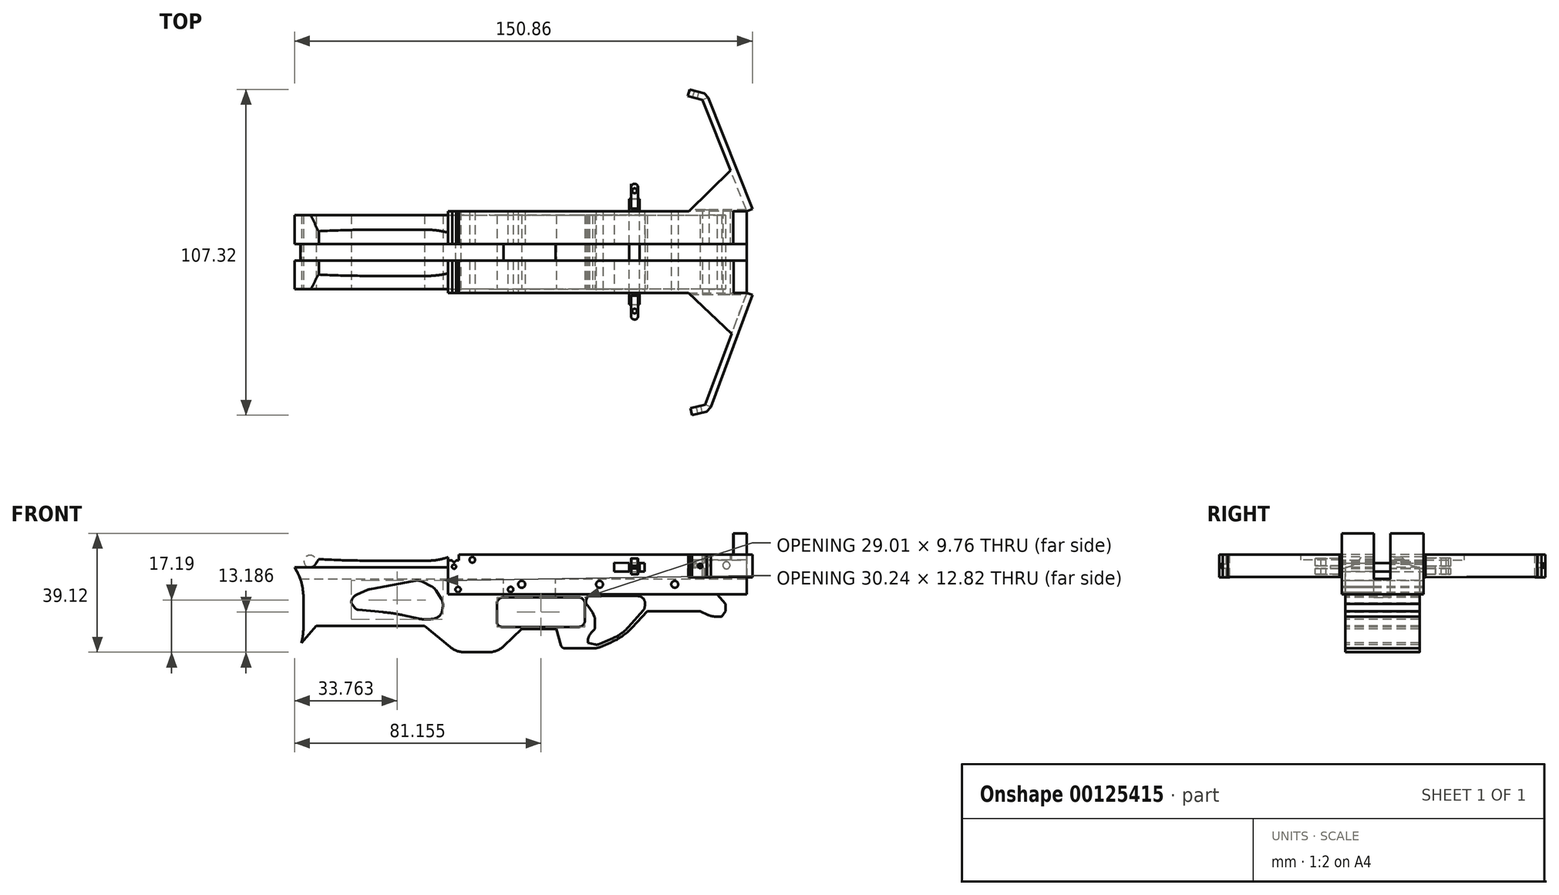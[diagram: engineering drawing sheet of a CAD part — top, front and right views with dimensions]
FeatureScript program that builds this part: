
annotation { "Feature Type Name" : "Feature", "Feature Type Description" : "" }
export const myFeature = defineFeature(function(context is Context, id is Id, definition is map)
    precondition{}
    {
        {
            var Q0;
            Q0=qCreatedBy(makeId("Top.planeOp"),FACE);
            var sketch = newSketch(context, id + "F0", { "sketchPlane" : qUnion([Q0])});
            skLineSegment(sketch, "E0", {"start": v(-24.32, 26.9) * mm, "end": v(-24.32, 0) * mm});
            skLineSegment(sketch, "E1", {"start": v(-24.32, 0) * mm, "end": v(74.17, 0) * mm});
            skLineSegment(sketch, "E2", {"start": v(74.17, 0) * mm, "end": v(74.17, 26.9) * mm});
            skLineSegment(sketch, "E3", {"start": v(74.17, 26.9) * mm, "end": v(-24.32, 26.9) * mm});
            skSolve(sketch);
        }
        {
            var Q0;
            Q0 = qSketchRegion(id + "F0", true);
            extrude(context, id + "F1", {"entities" : qUnion([Q0]), "depth" : 13 * mm});
        }
        {
            var Q0;
            Q0=makeQuery(id+"F1.opExtrude","CAP_FACE",FACE,{"disambiguationData":[OSD([sQuery(id+"F0.wireOp",EDGE,"E0"),sQuery(id+"F0.wireOp",EDGE,"E1"),sQuery(id+"F0.wireOp",EDGE,"E2"),sQuery(id+"F0.wireOp",EDGE,"E3")])],"isStart":false});
            var sketch = newSketch(context, id + "F2", { "sketchPlane" : qUnion([Q0])});
            skLineSegment(sketch, "E4.bottom", {"start": v(-24.32, 16.02) * mm, "end": v(74.17, 16.02) * mm});
            skLineSegment(sketch, "E4.top", {"start": v(-24.32, 10.62) * mm, "end": v(74.17, 10.62) * mm});
            skLineSegment(sketch, "E4.left", {"start": v(-24.32, 16.02) * mm, "end": v(-24.32, 10.62) * mm});
            skLineSegment(sketch, "E4.right", {"start": v(74.17, 16.02) * mm, "end": v(74.17, 10.62) * mm});
            skSolve(sketch);
        }
        {
            var Q0;
            Q0 = qSketchRegion(id + "F2", true);
            extrude(context, id + "F3", {"entities" : qUnion([Q0]), "operationType" : NewBodyOperationType.REMOVE, "oppositeDirection" : true, "depth" : 8 * mm});
        }
        {
            var Q0;
            Q0=makeQuery(id+"F1.opExtrude","SWEPT_FACE",FACE,{"disambiguationData":[OSD([sQuery(id+"F0.wireOp",EDGE,"E1")])]});
            var sketch = newSketch(context, id + "F4", { "sketchPlane" : qUnion([Q0])});
            skLineSegment(sketch, "E5", {"start": v(30.43, 10.33) * mm, "end": v(30.43, 7.4) * mm});
            skLineSegment(sketch, "E6", {"start": v(30.43, 7.4) * mm, "end": v(40.53, 7.4) * mm});
            skLineSegment(sketch, "E7", {"start": v(40.53, 7.4) * mm, "end": v(40.53, 10.23) * mm});
            skLineSegment(sketch, "E8", {"start": v(40.53, 10.23) * mm, "end": v(30.43, 10.33) * mm});
            skSolve(sketch);
        }
        {
            var Q0;
            Q0 = qSketchRegion(id + "F4", true);
            extrude(context, id + "F5", {"entities" : qUnion([Q0]), "operationType" : NewBodyOperationType.REMOVE, "oppositeDirection" : true, "depth" : 30 * mm});
        }
        {
            var Q0;
            Q0=makeQuery(id+"F1.opExtrude","SWEPT_FACE",FACE,{"disambiguationData":[OSD([sQuery(id+"F0.wireOp",EDGE,"E1")])]});
            var sketch = newSketch(context, id + "F6", { "sketchPlane" : qUnion([Q0])});
            skLineSegment(sketch, "E9", {"start": v(57.11, 13) * mm, "end": v(57.11, 5.6) * mm});
            skLineSegment(sketch, "E10", {"start": v(57.11, 5.6) * mm, "end": v(74.17, 5.6) * mm});
            skLineSegment(sketch, "E11", {"start": v(74.17, 5.6) * mm, "end": v(74.17, 13) * mm});
            skLineSegment(sketch, "E12", {"start": v(74.17, 13) * mm, "end": v(57.11, 13) * mm});
            skSolve(sketch);
        }
        {
            var Q0;
            Q0 = qSketchRegion(id + "F6", true);
            extrude(context, id + "F7", {"entities" : qUnion([Q0]), "operationType" : NewBodyOperationType.ADD, "depth" : 0.5 * mm});
        }
        {
            var Q0;
            Q0=makeQuery(id+"F1.opExtrude","SWEPT_FACE",FACE,{"disambiguationData":[OSD([sQuery(id+"F0.wireOp",EDGE,"E3")])]});
            var sketch = newSketch(context, id + "F8", { "sketchPlane" : qUnion([Q0])});
            skLineSegment(sketch, "E13", {"start": v(-74.17, 13) * mm, "end": v(-74.17, 5.6) * mm});
            skLineSegment(sketch, "E14", {"start": v(-74.17, 5.6) * mm, "end": v(-55.11, 5.6) * mm});
            skLineSegment(sketch, "E15", {"start": v(-55.11, 5.6) * mm, "end": v(-55.11, 13) * mm});
            skLineSegment(sketch, "E16", {"start": v(-55.11, 13) * mm, "end": v(-74.17, 13) * mm});
            skSolve(sketch);
        }
        {
            var Q0;
            Q0 = qSketchRegion(id + "F8", true);
            extrude(context, id + "F9", {"entities" : qUnion([Q0]), "operationType" : NewBodyOperationType.ADD, "depth" : 0.5 * mm});
        }
        {
            var Q0;
            Q0=makeQuery(id+"F7.opExtrude","CAP_FACE",FACE,{"disambiguationData":[OSD([sQuery(id+"F6.wireOp",EDGE,"E9"),sQuery(id+"F6.wireOp",EDGE,"E10"),sQuery(id+"F6.wireOp",EDGE,"E11"),sQuery(id+"F6.wireOp",EDGE,"E12")])],"isStart":false});
            var sketch = newSketch(context, id + "F10", { "sketchPlane" : qUnion([Q0])});
            skCircle(sketch, "E17", {"center": v(60.6, 9.48) * mm, "radius": 1.05 * mm});
            skCircle(sketch, "E18", {"center": v(67.47, 9.48) * mm, "radius": 1.18 * mm});
            skSolve(sketch);
        }
        {
            var Q0;
            Q0 = qSketchRegion(id + "F10", true);
            extrude(context, id + "F11", {"entities" : qUnion([Q0]), "operationType" : NewBodyOperationType.REMOVE, "oppositeDirection" : true, "depth" : 28.5 * mm});
        }
        {
            var Q0;
            Q0=makeQuery(id+"F1.opExtrude","SWEPT_FACE",FACE,{"disambiguationData":[OSD([sQuery(id+"F0.wireOp",EDGE,"E1")])]});
            var sketch = newSketch(context, id + "F12", { "sketchPlane" : qUnion([Q0])});
            skCircle(sketch, "E19", {"center": v(-20.96, 1.54) * mm, "radius": 0.9 * mm});
            skCircle(sketch, "E20", {"center": v(-3.64, 1.54) * mm, "radius": 0.9 * mm});
            skCircle(sketch, "E21", {"center": v(0, 3.23) * mm, "radius": 1.15 * mm});
            skCircle(sketch, "E22", {"center": v(25.65, 3.23) * mm, "radius": 1.14 * mm});
            skCircle(sketch, "E23", {"center": v(50.44, 3.23) * mm, "radius": 1.14 * mm});
            skSolve(sketch);
        }
        {
            var Q0;
            Q0 = qSketchRegion(id + "F12", true);
            extrude(context, id + "F13", {"entities" : qUnion([Q0]), "operationType" : NewBodyOperationType.REMOVE, "oppositeDirection" : true, "depth" : 28.5 * mm});
        }
        {
            var Q0;
            Q0=makeQuery(id+"F1.opExtrude","SWEPT_FACE",FACE,{"disambiguationData":[OSD([sQuery(id+"F0.wireOp",EDGE,"E3")])]});
            var sketch = newSketch(context, id + "F14", { "sketchPlane" : qUnion([Q0])});
            skLineSegment(sketch, "E24", {"start": v(-38.9, 10.24) * mm, "end": v(-38.87, 7.4) * mm});
            skPoint(sketch, "E24.endSnap0", {"position": v(-35.48, 7.4) * mm});
            skLineSegment(sketch, "E25", {"start": v(-38.87, 7.4) * mm, "end": v(-35.48, 7.4) * mm});
            skLineSegment(sketch, "E26", {"start": v(-35.48, 7.4) * mm, "end": v(-35.48, 10.28) * mm});
            skLineSegment(sketch, "E27", {"start": v(-35.48, 10.28) * mm, "end": v(-38.9, 10.24) * mm});
            skSolve(sketch);
        }
        {
            var Q0;
            Q0 = qSketchRegion(id + "F14", true);
            extrude(context, id + "F15", {"entities" : qUnion([Q0]), "operationType" : NewBodyOperationType.ADD, "oppositeDirection" : true, "depth" : 26.9 * mm});
        }
        {
            var Q0;
            Q0=makeQuery(id+"F15.boolean.opBoolean","MERGE",FACE,{"derivedFrom":[makeQuery(id+"F1.opExtrude","SWEPT_FACE",FACE,{"disambiguationData":[OSD([sQuery(id+"F0.wireOp",EDGE,"E3")])]}),makeQuery(id+"F15.opExtrude","CAP_FACE",FACE,{"disambiguationData":[OSD([sQuery(id+"F14.wireOp",EDGE,"E24"),sQuery(id+"F14.wireOp",EDGE,"E25"),sQuery(id+"F14.wireOp",EDGE,"E26"),sQuery(id+"F14.wireOp",EDGE,"E27")])],"isStart":true})]});
            var sketch = newSketch(context, id + "F16", { "sketchPlane" : qUnion([Q0])});
            skLineSegment(sketch, "E28.bottom", {"start": v(-38.9, 9.28) * mm, "end": v(-35.48, 9.28) * mm});
            skLineSegment(sketch, "E28.top", {"start": v(-38.9, 8.44) * mm, "end": v(-35.48, 8.44) * mm});
            skLineSegment(sketch, "E28.left", {"start": v(-38.9, 9.28) * mm, "end": v(-38.9, 8.44) * mm});
            skLineSegment(sketch, "E28.right", {"start": v(-35.48, 9.28) * mm, "end": v(-35.48, 8.44) * mm});
            skSolve(sketch);
        }
        {
            var Q0;
            Q0 = qSketchRegion(id + "F16", true);
            extrude(context, id + "F17", {"entities" : qUnion([Q0]), "operationType" : NewBodyOperationType.ADD, "depth" : 4 * mm});
        }
        {
            var Q0;
            Q0=makeQuery(id+"F17.opExtrude","SWEPT_FACE",FACE,{"disambiguationData":[OSD([sQuery(id+"F16.wireOp",EDGE,"E28.bottom")])]});
            var sketch = newSketch(context, id + "F18", { "sketchPlane" : qUnion([Q0])});
            skSolve(sketch);
        }
        {
            var Q0;
            {var subQ0=sQuery(id+"F16.wireOp",EDGE,"E28.bottom");Q0=makeQuery(id+"F18.imprint","IMPRINT",FACE,{"disambiguationData":[TD([[makeQuery(id+"F18.imprint","IMPRINT",EDGE,{"derivedFrom":makeQuery(id+"F17.opExtrude","CAP_EDGE",EDGE,{"disambiguationData":[OSD([subQ0])],"isStart":false})}),1.0]])]});}
            var sketch = newSketch(context, id + "F19", { "sketchPlane" : qUnion([Q0])});
            skLineSegment(sketch, "E29", {"start": v(38.29, 30.89) * mm, "end": v(38.29, 27.83) * mm});
            skLineSegment(sketch, "E30", {"start": v(38.16, 27.7) * mm, "end": v(36.22, 27.7) * mm});
            skLineSegment(sketch, "E31", {"start": v(36.1, 27.83) * mm, "end": v(36.1, 30.88) * mm});
            skLineSegment(sketch, "E32", {"start": v(36.1, 30.88) * mm, "end": v(38.29, 30.89) * mm});
            skPoint(sketch, "E33.visualSharp", {"position": v(38.29, 27.7) * mm});
            skArc(sketch, "E33.filletArc", {"start": v(38.16, 27.7) * mm, "mid": v(38.25, 27.74) * mm, "end": v(38.29, 27.83) * mm});
            skPoint(sketch, "E34.visualSharp", {"position": v(36.1, 27.7) * mm});
            skArc(sketch, "E34.filletArc", {"start": v(36.1, 27.83) * mm, "mid": v(36.13, 27.74) * mm, "end": v(36.22, 27.7) * mm});
            skSolve(sketch);
        }
        {
            var Q0;
            Q0=makeQuery(id+"F15.opExtrude","CAP_FACE",FACE,{"disambiguationData":[OSD([sQuery(id+"F14.wireOp",EDGE,"E24"),sQuery(id+"F14.wireOp",EDGE,"E25"),sQuery(id+"F14.wireOp",EDGE,"E26"),sQuery(id+"F14.wireOp",EDGE,"E27")])],"isStart":false});
            var sketch = newSketch(context, id + "F20", { "sketchPlane" : qUnion([Q0])});
            skLineSegment(sketch, "E35.bottom", {"start": v(35.48, 9.32) * mm, "end": v(38.88, 9.32) * mm});
            skLineSegment(sketch, "E35.top", {"start": v(35.48, 8.45) * mm, "end": v(38.88, 8.45) * mm});
            skLineSegment(sketch, "E35.left", {"start": v(35.48, 9.32) * mm, "end": v(35.48, 8.45) * mm});
            skLineSegment(sketch, "E35.right", {"start": v(38.88, 9.32) * mm, "end": v(38.88, 8.45) * mm});
            skSolve(sketch);
        }
        {
            var Q0;
            Q0 = qSketchRegion(id + "F20", true);
            extrude(context, id + "F21", {"entities" : qUnion([Q0]), "operationType" : NewBodyOperationType.ADD, "depth" : 3.8 * mm});
        }
        {
            var Q0;
            Q0=makeQuery(id+"F21.opExtrude","SWEPT_FACE",FACE,{"disambiguationData":[OSD([sQuery(id+"F20.wireOp",EDGE,"E35.bottom")])]});
            var sketch = newSketch(context, id + "F22", { "sketchPlane" : qUnion([Q0])});
            skLineSegment(sketch, "E36", {"start": v(36.04, -3.8) * mm, "end": v(36.04, -1.03) * mm});
            skLineSegment(sketch, "E37", {"start": v(36.17, -0.9) * mm, "end": v(38.18, -0.9) * mm});
            skLineSegment(sketch, "E38", {"start": v(38.3, -1.03) * mm, "end": v(38.3, -3.8) * mm});
            skLineSegment(sketch, "E39", {"start": v(38.3, -3.8) * mm, "end": v(36.04, -3.8) * mm});
            skPoint(sketch, "E40.visualSharp", {"position": v(36.04, -0.9) * mm});
            skArc(sketch, "E40.filletArc", {"start": v(36.17, -0.9) * mm, "mid": v(36.08, -0.94) * mm, "end": v(36.04, -1.03) * mm});
            skPoint(sketch, "E41.visualSharp", {"position": v(38.3, -0.9) * mm});
            skArc(sketch, "E41.filletArc", {"start": v(38.3, -1.03) * mm, "mid": v(38.27, -0.94) * mm, "end": v(38.18, -0.9) * mm});
            skSolve(sketch);
        }
        {
            var Q0;
            Q0 = qSketchRegion(id + "F22", true);
            extrude(context, id + "F23", {"entities" : qUnion([Q0]), "operationType" : NewBodyOperationType.ADD, "depth" : 2.4 * mm, "hasSecondDirection" : true, "secondDirectionOppositeDirection" : true, "secondDirectionDepth" : 2.8 * mm});
        }
        {
            var Q0;
            Q0 = qSketchRegion(id + "F19", true);
            extrude(context, id + "F24", {"entities" : qUnion([Q0]), "operationType" : NewBodyOperationType.ADD, "depth" : 2.6 * mm, "hasSecondDirection" : true, "secondDirectionOppositeDirection" : true, "secondDirectionDepth" : 2.75 * mm});
        }
        {
            var Q0;
            Q0=makeQuery(id+"F23.boolean.opBoolean","MERGE",FACE,{"derivedFrom":[makeQuery(id+"F21.opExtrude","CAP_FACE",FACE,{"disambiguationData":[OSD([sQuery(id+"F20.wireOp",EDGE,"E35.bottom"),sQuery(id+"F20.wireOp",EDGE,"E35.top"),sQuery(id+"F20.wireOp",EDGE,"E35.left"),sQuery(id+"F20.wireOp",EDGE,"E35.right")])],"isStart":false}),makeQuery(id+"F23.opExtrude","SWEPT_FACE",FACE,{"disambiguationData":[OSD([sQuery(id+"F22.wireOp",EDGE,"E39")])]})]});
            var sketch = newSketch(context, id + "F25", { "sketchPlane" : qUnion([Q0])});
            skLineSegment(sketch, "E42", {"start": v(36.04, 9.32) * mm, "end": v(38.3, 9.32) * mm});
            skLineSegment(sketch, "E43", {"start": v(38.3, 9.32) * mm, "end": v(38.3, 11.72) * mm});
            skLineSegment(sketch, "E44", {"start": v(38.3, 11.72) * mm, "end": v(36.04, 11.72) * mm});
            skLineSegment(sketch, "E45", {"start": v(36.04, 11.72) * mm, "end": v(36.04, 9.32) * mm});
            skLineSegment(sketch, "E46", {"start": v(36.04, 6.52) * mm, "end": v(36.04, 8.45) * mm});
            skLineSegment(sketch, "E47", {"start": v(36.04, 8.45) * mm, "end": v(38.3, 8.45) * mm});
            skLineSegment(sketch, "E48", {"start": v(38.3, 8.45) * mm, "end": v(38.3, 6.52) * mm});
            skLineSegment(sketch, "E49", {"start": v(38.3, 6.52) * mm, "end": v(36.04, 6.52) * mm});
            skSolve(sketch);
        }
        {
            var Q0;
            Q0 = qSketchRegion(id + "F25", true);
            extrude(context, id + "F26", {"entities" : qUnion([Q0]), "operationType" : NewBodyOperationType.ADD, "depth" : 5 * mm});
        }
        {
            var Q0;
            {var subQ1=sQuery(id+"F19.wireOp",EDGE,"E32");Q0=makeQuery(id+"F24.boolean.opBoolean","SPLIT",FACE,{"disambiguationData":[TD([makeQuery(id+"F17.opExtrude","SWEPT_FACE",FACE,{"disambiguationData":[OSD([sQuery(id+"F16.wireOp",EDGE,"E28.bottom")])]})])],"derivedFrom":makeQuery(id+"F24.opExtrude","SWEPT_FACE",FACE,{"disambiguationData":[OSD([subQ1])]})});}
            var sketch = newSketch(context, id + "F27", { "sketchPlane" : qUnion([Q0])});
            skLineSegment(sketch, "E50", {"start": v(-38.38, 9.28) * mm, "end": v(-38.38, 11.88) * mm});
            skLineSegment(sketch, "E51", {"start": v(-38.38, 11.88) * mm, "end": v(-36.2, 11.88) * mm});
            skLineSegment(sketch, "E52", {"start": v(-36.2, 11.88) * mm, "end": v(-36.2, 9.28) * mm});
            skLineSegment(sketch, "E53", {"start": v(-36.2, 9.28) * mm, "end": v(-38.38, 9.28) * mm});
            skLineSegment(sketch, "E54", {"start": v(-38.39, 8.42) * mm, "end": v(-38.39, 6.54) * mm});
            skLineSegment(sketch, "E55", {"start": v(-38.39, 6.54) * mm, "end": v(-36.21, 6.54) * mm});
            skLineSegment(sketch, "E56", {"start": v(-36.21, 6.54) * mm, "end": v(-36.21, 8.44) * mm});
            skLineSegment(sketch, "E57", {"start": v(-36.21, 8.44) * mm, "end": v(-38.39, 8.42) * mm});
            skSolve(sketch);
        }
        {
            var Q0;
            Q0 = qSketchRegion(id + "F27", true);
            extrude(context, id + "F28", {"entities" : qUnion([Q0]), "operationType" : NewBodyOperationType.ADD, "depth" : 5 * mm});
        }
        {
            var Q0;
            Q0 = qSketchRegion(id + "F27", true);
            extrude(context, id + "F29", {"entities" : qUnion([Q0]), "operationType" : NewBodyOperationType.ADD, "depth" : 5 * mm});
        }
        {
            var Q0;
            Q0=makeQuery(id+"F26.boolean.opBoolean","MERGE",FACE,{"derivedFrom":[makeQuery(id+"F23.opExtrude","CAP_FACE",FACE,{"disambiguationData":[OSD([sQuery(id+"F22.wireOp",EDGE,"E36"),sQuery(id+"F22.wireOp",EDGE,"E37"),sQuery(id+"F22.wireOp",EDGE,"E38"),sQuery(id+"F22.wireOp",EDGE,"E39"),sQuery(id+"F22.wireOp",EDGE,"E40.filletArc"),sQuery(id+"F22.wireOp",EDGE,"E41.filletArc")])],"isStart":false}),makeQuery(id+"F26.opExtrude","SWEPT_FACE",FACE,{"disambiguationData":[OSD([sQuery(id+"F25.wireOp",EDGE,"E44")])]})]});
            var sketch = newSketch(context, id + "F30", { "sketchPlane" : qUnion([Q0])});
            skLineSegment(sketch, "E58", {"start": v(38.3, -7.34) * mm, "end": v(36.04, -7.34) * mm});
            skLineSegment(sketch, "E59", {"start": v(36.04, -7.34) * mm, "end": v(36.04, -7.68) * mm});
            skLineSegment(sketch, "E60", {"start": v(37.16, -8.8) * mm, "end": v(37.32, -8.8) * mm});
            skLineSegment(sketch, "E61", {"start": v(38.3, -7.81) * mm, "end": v(38.3, -7.34) * mm});
            skPoint(sketch, "E62.visualSharp", {"position": v(38.3, -8.8) * mm});
            skArc(sketch, "E62.filletArc", {"start": v(37.32, -8.8) * mm, "mid": v(38.01, -8.5) * mm, "end": v(38.3, -7.81) * mm});
            skPoint(sketch, "E63.visualSharp", {"position": v(36.04, -8.8) * mm});
            skArc(sketch, "E63.filletArc", {"start": v(36.04, -7.68) * mm, "mid": v(36.37, -8.47) * mm, "end": v(37.16, -8.8) * mm});
            skSolve(sketch);
        }
        {
            var Q0;
            {var subQ0=sQuery(id+"F30.wireOp",EDGE,"E62.filletArc");Q0=makeQuery(id+"F30.imprint","IMPRINT",FACE,{"disambiguationData":[TD([[makeQuery(id+"F30.imprint","IMPRINT",EDGE,{"derivedFrom":subQ0}),-1.0]])]});}
            var Q1;
            {var subQ0=sQuery(id+"F30.wireOp",EDGE,"E63.filletArc");Q1=makeQuery(id+"F30.imprint","IMPRINT",FACE,{"disambiguationData":[TD([[makeQuery(id+"F30.imprint","IMPRINT",EDGE,{"derivedFrom":subQ0}),-1.0]])]});}
            extrude(context, id + "F31", {"entities" : qUnion([Q0, Q1]), "operationType" : NewBodyOperationType.REMOVE, "oppositeDirection" : true, "depth" : 25 * mm});
        }
        {
            var Q0;
            Q0=makeQuery(id+"F28.opExtrude","SWEPT_FACE",FACE,{"disambiguationData":[OSD([sQuery(id+"F27.wireOp",EDGE,"E55")])]});
            var sketch = newSketch(context, id + "F32", { "sketchPlane" : qUnion([Q0])});
            skLineSegment(sketch, "E64.bottom", {"start": v(37, -35.88) * mm, "end": v(37.39, -35.88) * mm});
            skLineSegment(sketch, "E64.top", {"start": v(36.1, -33.39) * mm, "end": v(38.29, -33.39) * mm});
            skLineSegment(sketch, "E64.left", {"start": v(36.1, -34.98) * mm, "end": v(36.1, -33.39) * mm});
            skLineSegment(sketch, "E64.right", {"start": v(38.29, -34.98) * mm, "end": v(38.29, -33.39) * mm});
            skPoint(sketch, "E65.visualSharp", {"position": v(38.29, -35.88) * mm});
            skArc(sketch, "E65.filletArc", {"start": v(37.39, -35.88) * mm, "mid": v(38.02, -35.62) * mm, "end": v(38.29, -34.98) * mm});
            skPoint(sketch, "E66.visualSharp", {"position": v(36.1, -35.88) * mm});
            skArc(sketch, "E66.filletArc", {"start": v(36.1, -34.98) * mm, "mid": v(36.37, -35.62) * mm, "end": v(37, -35.88) * mm});
            skSolve(sketch);
        }
        {
            var Q0;
            {var subQ3=sQuery(id+"F32.wireOp",EDGE,"E64.bottom");Q0=makeQuery(id+"F32.imprint","IMPRINT",FACE,{"disambiguationData":[TD([[makeQuery(id+"F32.imprint","IMPRINT",EDGE,{"derivedFrom":subQ3}),-1.0]])]});}
            extrude(context, id + "F33", {"entities" : qUnion([Q0]), "operationType" : NewBodyOperationType.REMOVE, "oppositeDirection" : true, "depth" : 25 * mm});
        }
        {
            var Q0;
            Q0=makeQuery(id+"F1.opExtrude","SWEPT_FACE",FACE,{"disambiguationData":[OSD([sQuery(id+"F0.wireOp",EDGE,"E1")])]});
            var sketch = newSketch(context, id + "F34", { "sketchPlane" : qUnion([Q0])});
            skCircle(sketch, "E67", {"center": v(-22.28, 11.3) * mm, "radius": 0.69 * mm});
            skCircle(sketch, "E68", {"center": v(-22.28, 9.06) * mm, "radius": 0.69 * mm});
            skCircle(sketch, "E69", {"center": v(-16.26, 11.3) * mm, "radius": 0.92 * mm});
            skSolve(sketch);
        }
        {
            var Q0;
            Q0 = qSketchRegion(id + "F34", true);
            extrude(context, id + "F35", {"entities" : qUnion([Q0]), "operationType" : NewBodyOperationType.REMOVE, "oppositeDirection" : true, "depth" : 27.5 * mm});
        }
        {
            var Q0;
            Q0=makeQuery(id+"F1.opExtrude","SWEPT_FACE",FACE,{"disambiguationData":[OSD([sQuery(id+"F0.wireOp",EDGE,"E1")])]});
            var sketch = newSketch(context, id + "F36", { "sketchPlane" : qUnion([Q0])});
            skLineSegment(sketch, "E70.bottom", {"start": v(54.94, 13) * mm, "end": v(57.11, 13) * mm});
            skLineSegment(sketch, "E70.top", {"start": v(54.94, 5.6) * mm, "end": v(57.11, 5.6) * mm});
            skLineSegment(sketch, "E70.left", {"start": v(54.94, 13) * mm, "end": v(54.94, 5.6) * mm});
            skLineSegment(sketch, "E70.right", {"start": v(57.11, 13) * mm, "end": v(57.11, 5.6) * mm});
            skSolve(sketch);
        }
        {
            var Q0;
            Q0 = qSketchRegion(id + "F36", true);
            extrude(context, id + "F37", {"entities" : qUnion([Q0]), "operationType" : NewBodyOperationType.ADD, "depth" : 0.5 * mm});
        }
        {
            var Q0;
            Q0=makeQuery(id+"F9.opExtrude","CAP_FACE",FACE,{"disambiguationData":[OSD([sQuery(id+"F8.wireOp",EDGE,"E13"),sQuery(id+"F8.wireOp",EDGE,"E14"),sQuery(id+"F8.wireOp",EDGE,"E15"),sQuery(id+"F8.wireOp",EDGE,"E16")])],"isStart":false});
            var sketch = newSketch(context, id + "F38", { "sketchPlane" : qUnion([Q0])});
            skLineSegment(sketch, "E71.bottom", {"start": v(-74.17, 13) * mm, "end": v(-55.11, 13) * mm});
            skLineSegment(sketch, "E71.top", {"start": v(-74.17, 11.22) * mm, "end": v(-55.11, 11.22) * mm});
            skLineSegment(sketch, "E71.left", {"start": v(-74.17, 13) * mm, "end": v(-74.17, 11.22) * mm});
            skLineSegment(sketch, "E71.right", {"start": v(-55.11, 13) * mm, "end": v(-55.11, 11.22) * mm});
            skSolve(sketch);
        }
        {
            var Q0;
            Q0 = qSketchRegion(id + "F38", true);
            extrude(context, id + "F39", {"entities" : qUnion([Q0]), "operationType" : NewBodyOperationType.ADD, "depth" : 13 * mm});
        }
        {
            var Q0;
            Q0=makeQuery(id+"F37.boolean.opBoolean","MERGE",FACE,{"derivedFrom":[makeQuery(id+"F7.opExtrude","CAP_FACE",FACE,{"disambiguationData":[OSD([sQuery(id+"F6.wireOp",EDGE,"E9"),sQuery(id+"F6.wireOp",EDGE,"E10"),sQuery(id+"F6.wireOp",EDGE,"E11"),sQuery(id+"F6.wireOp",EDGE,"E12")])],"isStart":false}),makeQuery(id+"F37.opExtrude","CAP_FACE",FACE,{"disambiguationData":[OSD([sQuery(id+"F36.wireOp",EDGE,"E70.bottom"),sQuery(id+"F36.wireOp",EDGE,"E70.top"),sQuery(id+"F36.wireOp",EDGE,"E70.left"),sQuery(id+"F36.wireOp",EDGE,"E70.right")])],"isStart":false})]});
            var sketch = newSketch(context, id + "F40", { "sketchPlane" : qUnion([Q0])});
            skLineSegment(sketch, "E72.bottom", {"start": v(54.94, 13) * mm, "end": v(74.17, 13) * mm});
            skLineSegment(sketch, "E72.top", {"start": v(54.94, 11.27) * mm, "end": v(74.17, 11.27) * mm});
            skLineSegment(sketch, "E72.left", {"start": v(54.94, 13) * mm, "end": v(54.94, 11.27) * mm});
            skLineSegment(sketch, "E72.right", {"start": v(74.17, 13) * mm, "end": v(74.17, 11.27) * mm});
            skSolve(sketch);
        }
        {
            var Q0;
            Q0 = qSketchRegion(id + "F40", true);
            extrude(context, id + "F41", {"entities" : qUnion([Q0]), "operationType" : NewBodyOperationType.ADD, "depth" : 13 * mm});
        }
        {
            var Q0;
            {var subQ0=sQuery(id+"F0.wireOp",EDGE,"E0");var subQ1=sQuery(id+"F0.wireOp",EDGE,"E2");var subQ2=sQuery(id+"F0.wireOp",EDGE,"E3");Q0=makeQuery(id+"F39.boolean.opBoolean","MERGE",FACE,{"derivedFrom":[makeQuery(id+"F9.boolean.opBoolean","MERGE",FACE,{"derivedFrom":[makeQuery(id+"F3.boolean.opBoolean","SPLIT",FACE,{"disambiguationData":[TD([makeQuery(id+"F1.opExtrude","SWEPT_FACE",FACE,{"disambiguationData":[OSD([subQ2])]})])],"derivedFrom":makeQuery(id+"F1.opExtrude","CAP_FACE",FACE,{"disambiguationData":[OSD([subQ0,sQuery(id+"F0.wireOp",EDGE,"E1"),subQ1,subQ2])],"isStart":false})}),makeQuery(id+"F9.opExtrude","SWEPT_FACE",FACE,{"disambiguationData":[OSD([sQuery(id+"F8.wireOp",EDGE,"E16")])]})]}),makeQuery(id+"F39.opExtrude","SWEPT_FACE",FACE,{"disambiguationData":[OSD([sQuery(id+"F38.wireOp",EDGE,"E71.bottom")])]})]});}
            var sketch = newSketch(context, id + "F42", { "sketchPlane" : qUnion([Q0])});
            skLineSegment(sketch, "E73", {"start": v(74.17, 26.9) * mm, "end": v(68.81, 40.4) * mm});
            skLineSegment(sketch, "E74", {"start": v(68.81, 40.4) * mm, "end": v(74.17, 40.4) * mm});
            skLineSegment(sketch, "E75", {"start": v(74.17, 40.4) * mm, "end": v(74.17, 26.9) * mm});
            skLineSegment(sketch, "E76", {"start": v(68.81, 40.4) * mm, "end": v(55.11, 26.9) * mm});
            skLineSegment(sketch, "E77", {"start": v(55.11, 26.9) * mm, "end": v(55.11, 40.4) * mm});
            skLineSegment(sketch, "E78", {"start": v(55.11, 40.4) * mm, "end": v(68.81, 40.4) * mm});
            skSolve(sketch);
        }
        {
            var Q0;
            Q0 = qSketchRegion(id + "F42", true);
            extrude(context, id + "F43", {"entities" : qUnion([Q0]), "operationType" : NewBodyOperationType.REMOVE, "oppositeDirection" : true, "depth" : 25 * mm});
        }
        {
            var Q0;
            {var subQ0=sQuery(id+"F0.wireOp",EDGE,"E0");var subQ1=sQuery(id+"F0.wireOp",EDGE,"E1");var subQ2=sQuery(id+"F0.wireOp",EDGE,"E2");Q0=makeQuery(id+"F41.boolean.opBoolean","MERGE",FACE,{"derivedFrom":[makeQuery(id+"F37.boolean.opBoolean","MERGE",FACE,{"derivedFrom":[makeQuery(id+"F7.boolean.opBoolean","MERGE",FACE,{"derivedFrom":[makeQuery(id+"F3.boolean.opBoolean","SPLIT",FACE,{"disambiguationData":[TD([makeQuery(id+"F1.opExtrude","SWEPT_FACE",FACE,{"disambiguationData":[OSD([subQ1])]})])],"derivedFrom":makeQuery(id+"F1.opExtrude","CAP_FACE",FACE,{"disambiguationData":[OSD([subQ0,subQ1,subQ2,sQuery(id+"F0.wireOp",EDGE,"E3")])],"isStart":false})}),makeQuery(id+"F7.opExtrude","SWEPT_FACE",FACE,{"disambiguationData":[OSD([sQuery(id+"F6.wireOp",EDGE,"E12")])]})]}),makeQuery(id+"F37.opExtrude","SWEPT_FACE",FACE,{"disambiguationData":[OSD([sQuery(id+"F36.wireOp",EDGE,"E70.bottom")])]})]}),makeQuery(id+"F41.opExtrude","SWEPT_FACE",FACE,{"disambiguationData":[OSD([sQuery(id+"F40.wireOp",EDGE,"E72.bottom")])]})]});}
            var sketch = newSketch(context, id + "F44", { "sketchPlane" : qUnion([Q0])});
            skLineSegment(sketch, "E79", {"start": v(74.17, 0) * mm, "end": v(69.16, -13.5) * mm});
            skLineSegment(sketch, "E80", {"start": v(69.16, -13.5) * mm, "end": v(74.17, -13.5) * mm});
            skLineSegment(sketch, "E81", {"start": v(74.17, -13.5) * mm, "end": v(74.17, 0) * mm});
            skLineSegment(sketch, "E82", {"start": v(69.16, -13.5) * mm, "end": v(54.94, 0) * mm});
            skLineSegment(sketch, "E83", {"start": v(54.94, 0) * mm, "end": v(54.94, -13.5) * mm});
            skLineSegment(sketch, "E84", {"start": v(54.94, -13.5) * mm, "end": v(69.16, -13.5) * mm});
            skSolve(sketch);
        }
        {
            var Q0;
            Q0 = qSketchRegion(id + "F44", true);
            extrude(context, id + "F45", {"entities" : qUnion([Q0]), "operationType" : NewBodyOperationType.REMOVE, "oppositeDirection" : true, "depth" : 25 * mm});
        }
        {
            var Q0;
            Q0=makeQuery(id+"F1.opExtrude","SWEPT_FACE",FACE,{"disambiguationData":[OSD([sQuery(id+"F0.wireOp",EDGE,"E1")])]});
            var sketch = newSketch(context, id + "F46", { "sketchPlane" : qUnion([Q0])});
            skLineSegment(sketch, "E85.bottom", {"start": v(-24.32, 13) * mm, "end": v(-20.7, 13) * mm});
            skLineSegment(sketch, "E85.top", {"start": v(-24.32, 12.14) * mm, "end": v(-20.7, 12.14) * mm});
            skLineSegment(sketch, "E85.left", {"start": v(-24.32, 13) * mm, "end": v(-24.32, 12.14) * mm});
            skLineSegment(sketch, "E85.right", {"start": v(-20.7, 13) * mm, "end": v(-20.7, 12.14) * mm});
            skSolve(sketch);
        }
        {
            var Q0;
            Q0 = qSketchRegion(id + "F46", true);
            extrude(context, id + "F47", {"entities" : qUnion([Q0]), "operationType" : NewBodyOperationType.REMOVE, "oppositeDirection" : true, "depth" : 27.5 * mm});
        }
        {
            var Q0;
            Q0=makeQuery(id+"F1.opExtrude","SWEPT_FACE",FACE,{"disambiguationData":[OSD([sQuery(id+"F0.wireOp",EDGE,"E0")])]});
            var sketch = newSketch(context, id + "F48", { "sketchPlane" : qUnion([Q0])});
            skLineSegment(sketch, "E86", {"start": v(-25.64, 0) * mm, "end": v(-25.64, 12.14) * mm});
            skLineSegment(sketch, "E87", {"start": v(-25.64, 12.14) * mm, "end": v(-1.22, 12.14) * mm});
            skLineSegment(sketch, "E88", {"start": v(-1.22, 12.14) * mm, "end": v(-1.22, 0) * mm});
            skLineSegment(sketch, "E89", {"start": v(-1.22, 0) * mm, "end": v(-25.64, 0) * mm});
            skSolve(sketch);
        }
        {
            var Q0;
            {var subQ7=sQuery(id+"F48.wireOp",EDGE,"E86");Q0=makeQuery(id+"F48.imprint","IMPRINT",FACE,{"disambiguationData":[TD([[makeQuery(id+"F48.imprint","IMPRINT",EDGE,{"derivedFrom":subQ7}),-1.0]])]});}
            var Q1;
            {var subQ1=sQuery(id+"F2.wireOp",EDGE,"E4.left");Q1=makeQuery(id+"F48.imprint","IMPRINT",FACE,{"disambiguationData":[TD([[makeQuery(id+"F48.imprint","IMPRINT",EDGE,{"derivedFrom":makeQuery(id+"F3.boolean.opBoolean","COPY",EDGE,{"derivedFrom":makeQuery(id+"F3.opExtrude","CAP_EDGE",EDGE,{"disambiguationData":[OSD([subQ1])],"isStart":false})})}),1.0]])]});}
            extrude(context, id + "F49", {"entities" : qUnion([Q0, Q1]), "operationType" : NewBodyOperationType.ADD, "depth" : 50.5 * mm});
        }
        {
            var Q0;
            Q0=makeQuery(id+"F49.opExtrude","SWEPT_FACE",FACE,{"disambiguationData":[OSD([sQuery(id+"F48.wireOp",EDGE,"E88")])]});
            var sketch = newSketch(context, id + "F50", { "sketchPlane" : qUnion([Q0])});
            skLineSegment(sketch, "E90", {"start": v(-74.82, 12.14) * mm, "end": v(-69.82, 11.76) * mm});
            skLineSegment(sketch, "E91", {"start": v(-50.5, 11.04) * mm, "end": v(-30.67, 11.04) * mm});
            skLineSegment(sketch, "E92", {"start": v(-25.56, 11.78) * mm, "end": v(-24.32, 12.14) * mm});
            skLineSegment(sketch, "E93", {"start": v(-24.32, 12.14) * mm, "end": v(-74.82, 12.14) * mm});
            skPoint(sketch, "E94.visualSharp", {"position": v(-60.17, 11.04) * mm});
            skArc(sketch, "E94.filletArc", {"start": v(-69.82, 11.76) * mm, "mid": v(-60.16, 11.22) * mm, "end": v(-50.5, 11.04) * mm});
            skPoint(sketch, "E95.visualSharp", {"position": v(-28.06, 11.04) * mm});
            skArc(sketch, "E95.filletArc", {"start": v(-30.67, 11.04) * mm, "mid": v(-28.09, 11.23) * mm, "end": v(-25.56, 11.78) * mm});
            skSolve(sketch);
        }
        {
            var Q0;
            Q0=makeQuery(id+"F50.imprint","IMPRINT",FACE,{"disambiguationData":[TD([[makeQuery(id+"F50.imprint","IMPRINT",EDGE,{"derivedFrom":sQuery(id+"F50.wireOp",EDGE,"E90")}),1.0]])]});
            extrude(context, id + "F51", {"entities" : qUnion([Q0]), "operationType" : NewBodyOperationType.REMOVE, "oppositeDirection" : true, "depth" : 25 * mm});
        }
        {
            var Q0;
            Q0=makeQuery(id+"F49.opExtrude","CAP_FACE",FACE,{"disambiguationData":[OSD([sQuery(id+"F48.wireOp",EDGE,"E86"),sQuery(id+"F48.wireOp",EDGE,"E87"),sQuery(id+"F48.wireOp",EDGE,"E88"),sQuery(id+"F48.wireOp",EDGE,"E89")])],"isStart":false});
            var sketch = newSketch(context, id + "F52", { "sketchPlane" : qUnion([Q0])});
            skArc(sketch, "E96", {"start": v(-6.35, 12.14) * mm, "mid": v(-4.2, 9.83) * mm, "end": v(-1.22, 8.8) * mm});
            skArc(sketch, "E97", {"start": v(-25.64, 8.8) * mm, "mid": v(-22.37, 9.78) * mm, "end": v(-19.9, 12.14) * mm});
            skSolve(sketch);
        }
        {
            var Q0;
            {var subQ0=sQuery(id+"F52.wireOp",EDGE,"E97");Q0=makeQuery(id+"F52.imprint","IMPRINT",FACE,{"disambiguationData":[TD([[makeQuery(id+"F52.imprint","IMPRINT",EDGE,{"derivedFrom":subQ0}),1.0]])]});}
            var Q1;
            {var subQ0=sQuery(id+"F52.wireOp",EDGE,"E96");Q1=makeQuery(id+"F52.imprint","IMPRINT",FACE,{"disambiguationData":[TD([[makeQuery(id+"F52.imprint","IMPRINT",EDGE,{"derivedFrom":subQ0}),1.0]])]});}
            extrude(context, id + "F53", {"entities" : qUnion([Q0, Q1]), "operationType" : NewBodyOperationType.REMOVE, "oppositeDirection" : true, "depth" : 50.5 * mm});
        }
        {
            var Q0;
            Q0=makeQuery(id+"F49.opExtrude","SWEPT_FACE",FACE,{"disambiguationData":[OSD([sQuery(id+"F48.wireOp",EDGE,"E88")])]});
            var sketch = newSketch(context, id + "F54", { "sketchPlane" : qUnion([Q0])});
            skLineSegment(sketch, "E98", {"start": v(-74.82, 8.8) * mm, "end": v(-74.82, 12.2) * mm});
            skLineSegment(sketch, "E99", {"start": v(-74.82, 12.2) * mm, "end": v(-70, 11.77) * mm});
            skLineSegment(sketch, "E100", {"start": v(-70, 11.77) * mm, "end": v(-66.82, 11.6) * mm});
            skLineSegment(sketch, "E101", {"start": v(-66.82, 11.6) * mm, "end": v(-68.04, 9.72) * mm});
            skLineSegment(sketch, "E102", {"start": v(-69.72, 8.8) * mm, "end": v(-74.82, 8.8) * mm});
            skPoint(sketch, "E103.visualSharp", {"position": v(-68.63, 8.8) * mm});
            skArc(sketch, "E103.filletArc", {"start": v(-69.72, 8.8) * mm, "mid": v(-68.76, 9.04) * mm, "end": v(-68.04, 9.72) * mm});
            skSolve(sketch);
        }
        {
            var Q0;
            Q0=makeQuery(id+"F54.imprint","IMPRINT",FACE,{"disambiguationData":[TD([[makeQuery(id+"F54.imprint","IMPRINT",EDGE,{"derivedFrom":sQuery(id+"F54.wireOp",EDGE,"E98")}),-1.0]])]});
            extrude(context, id + "F55", {"entities" : qUnion([Q0]), "operationType" : NewBodyOperationType.REMOVE, "oppositeDirection" : true, "depth" : 25 * mm});
        }
        {
            var Q0;
            Q0=makeQuery(id+"F49.boolean.opBoolean","MERGE",FACE,{"derivedFrom":[makeQuery(id+"F1.opExtrude","CAP_FACE",FACE,{"disambiguationData":[OSD([sQuery(id+"F0.wireOp",EDGE,"E0"),sQuery(id+"F0.wireOp",EDGE,"E1"),sQuery(id+"F0.wireOp",EDGE,"E2"),sQuery(id+"F0.wireOp",EDGE,"E3")])],"isStart":true}),makeQuery(id+"F49.opExtrude","SWEPT_FACE",FACE,{"disambiguationData":[OSD([sQuery(id+"F48.wireOp",EDGE,"E89")])]})]});
            var sketch = newSketch(context, id + "F56", { "sketchPlane" : qUnion([Q0])});
            skLineSegment(sketch, "E104.bottom", {"start": v(67.18, -1.22) * mm, "end": v(-74.82, -1.22) * mm});
            skLineSegment(sketch, "E104.top", {"start": v(67.18, -25.64) * mm, "end": v(-74.82, -25.64) * mm});
            skLineSegment(sketch, "E104.left", {"start": v(67.18, -1.22) * mm, "end": v(67.18, -25.64) * mm});
            skLineSegment(sketch, "E104.right", {"start": v(-74.82, -1.22) * mm, "end": v(-74.82, -25.64) * mm});
            skSolve(sketch);
        }
        {
            var Q0;
            {var subQ10=sQuery(id+"F56.wireOp",EDGE,"E104.left");Q0=makeQuery(id+"F56.imprint","IMPRINT",FACE,{"disambiguationData":[TD([[makeQuery(id+"F56.imprint","IMPRINT",EDGE,{"derivedFrom":subQ10}),-1.0]])]});}
            extrude(context, id + "F57", {"entities" : qUnion([Q0]), "operationType" : NewBodyOperationType.ADD, "depth" : 21 * mm});
        }
        {
            var Q0;
            Q0=makeQuery(id+"F57.boolean.opBoolean","MERGE",FACE,{"derivedFrom":[makeQuery(id+"F49.opExtrude","SWEPT_FACE",FACE,{"disambiguationData":[OSD([sQuery(id+"F48.wireOp",EDGE,"E88")])]}),makeQuery(id+"F57.opExtrude","SWEPT_FACE",FACE,{"disambiguationData":[OSD([sQuery(id+"F56.wireOp",EDGE,"E104.bottom")])]})]});
            var sketch = newSketch(context, id + "F58", { "sketchPlane" : qUnion([Q0])});
            skLineSegment(sketch, "E105", {"start": v(-74.82, 8.8) * mm, "end": v(-74.34, 7.97) * mm});
            skLineSegment(sketch, "E106", {"start": v(-71.93, -0.95) * mm, "end": v(-71.93, -11.28) * mm});
            skLineSegment(sketch, "E107", {"start": v(-74.5, -20.48) * mm, "end": v(-74.82, -21) * mm});
            skLineSegment(sketch, "E108", {"start": v(-74.82, -21) * mm, "end": v(-74.82, 8.8) * mm});
            skPoint(sketch, "E109.visualSharp", {"position": v(-71.93, 3.84) * mm});
            skArc(sketch, "E109.filletArc", {"start": v(-71.93, -0.95) * mm, "mid": v(-72.55, 3.67) * mm, "end": v(-74.34, 7.97) * mm});
            skPoint(sketch, "E110.visualSharp", {"position": v(-71.93, -16.24) * mm});
            skArc(sketch, "E110.filletArc", {"start": v(-74.5, -20.48) * mm, "mid": v(-72.59, -16.05) * mm, "end": v(-71.93, -11.28) * mm});
            skSolve(sketch);
        }
        {
            var Q0;
            Q0=makeQuery(id+"F58.imprint","IMPRINT",FACE,{"disambiguationData":[TD([[makeQuery(id+"F58.imprint","IMPRINT",EDGE,{"derivedFrom":sQuery(id+"F58.wireOp",EDGE,"E105")}),-1.0]])]});
            extrude(context, id + "F59", {"entities" : qUnion([Q0]), "operationType" : NewBodyOperationType.REMOVE, "oppositeDirection" : true, "depth" : 25 * mm});
        }
        {
            var Q0;
            Q0=makeQuery(id+"F57.boolean.opBoolean","MERGE",FACE,{"derivedFrom":[makeQuery(id+"F49.opExtrude","SWEPT_FACE",FACE,{"disambiguationData":[OSD([sQuery(id+"F48.wireOp",EDGE,"E88")])]}),makeQuery(id+"F57.opExtrude","SWEPT_FACE",FACE,{"disambiguationData":[OSD([sQuery(id+"F56.wireOp",EDGE,"E104.bottom")])]})]});
            var sketch = newSketch(context, id + "F60", { "sketchPlane" : qUnion([Q0])});
            skLineSegment(sketch, "E111", {"start": v(64.39, 0) * mm, "end": v(67.18, -3.2) * mm});
            skLineSegment(sketch, "E112", {"start": v(67.18, -3.2) * mm, "end": v(67.18, -5.7) * mm});
            skLineSegment(sketch, "E113", {"start": v(67.18, -5.7) * mm, "end": v(65.88, -7.38) * mm});
            skLineSegment(sketch, "E114", {"start": v(65.88, -7.38) * mm, "end": v(63.77, -7.38) * mm});
            skLineSegment(sketch, "E115", {"start": v(61.52, -6.9) * mm, "end": v(58.8, -5.7) * mm});
            skLineSegment(sketch, "E116", {"start": v(58.8, -5.7) * mm, "end": v(41.37, -5.7) * mm});
            skLineSegment(sketch, "E117", {"start": v(41.37, -5.7) * mm, "end": v(36.28, -11.1) * mm});
            skLineSegment(sketch, "E118", {"start": v(29.4, -15.9) * mm, "end": v(25.85, -17.42) * mm});
            skLineSegment(sketch, "E119", {"start": v(23.68, -17.87) * mm, "end": v(14.22, -17.87) * mm});
            skLineSegment(sketch, "E120", {"start": v(13, -16.95) * mm, "end": v(11.39, -11.47) * mm});
            skLineSegment(sketch, "E121", {"start": v(11.39, -11.47) * mm, "end": v(0, -11.47) * mm});
            skLineSegment(sketch, "E122", {"start": v(0, -11.47) * mm, "end": v(-5.83, -17.1) * mm});
            skLineSegment(sketch, "E123", {"start": v(-10.85, -19.12) * mm, "end": v(-18.9, -19.12) * mm});
            skLineSegment(sketch, "E124", {"start": v(-23.49, -17.48) * mm, "end": v(-32.02, -10.46) * mm});
            skLineSegment(sketch, "E125", {"start": v(-32.02, -10.46) * mm, "end": v(-50.09, -10.46) * mm});
            skLineSegment(sketch, "E126", {"start": v(-50.09, -10.46) * mm, "end": v(-67.65, -10.46) * mm});
            skLineSegment(sketch, "E127", {"start": v(-67.65, -10.46) * mm, "end": v(-72.59, -16.05) * mm});
            skLineSegment(sketch, "E128", {"start": v(-72.59, -16.05) * mm, "end": v(-74.5, -20.48) * mm});
            skLineSegment(sketch, "E129", {"start": v(-74.5, -20.48) * mm, "end": v(-74.82, -21) * mm});
            skLineSegment(sketch, "E130", {"start": v(-74.82, -21) * mm, "end": v(67.18, -21) * mm});
            skLineSegment(sketch, "E131", {"start": v(67.18, -21) * mm, "end": v(67.18, 0) * mm});
            skLineSegment(sketch, "E132", {"start": v(67.18, 0) * mm, "end": v(64.39, 0) * mm});
            skPoint(sketch, "E133.visualSharp", {"position": v(-7.93, -19.12) * mm});
            skArc(sketch, "E133.filletArc", {"start": v(-10.85, -19.12) * mm, "mid": v(-8.15, -18.6) * mm, "end": v(-5.83, -17.1) * mm});
            skPoint(sketch, "E134.visualSharp", {"position": v(-21.48, -19.12) * mm});
            skArc(sketch, "E134.filletArc", {"start": v(-23.49, -17.48) * mm, "mid": v(-21.33, -18.7) * mm, "end": v(-18.9, -19.12) * mm});
            skPoint(sketch, "E135.visualSharp", {"position": v(13.27, -17.87) * mm});
            skArc(sketch, "E135.filletArc", {"start": v(13, -16.95) * mm, "mid": v(13.46, -17.61) * mm, "end": v(14.22, -17.87) * mm});
            skPoint(sketch, "E136.visualSharp", {"position": v(24.81, -17.87) * mm});
            skArc(sketch, "E136.filletArc", {"start": v(23.68, -17.87) * mm, "mid": v(24.79, -17.75) * mm, "end": v(25.85, -17.42) * mm});
            skPoint(sketch, "E137.visualSharp", {"position": v(62.6, -7.38) * mm});
            skArc(sketch, "E137.filletArc", {"start": v(61.52, -6.9) * mm, "mid": v(62.62, -7.26) * mm, "end": v(63.77, -7.38) * mm});
            skPoint(sketch, "E138.visualSharp", {"position": v(33.34, -14.23) * mm});
            skArc(sketch, "E138.filletArc", {"start": v(29.4, -15.9) * mm, "mid": v(33.09, -13.86) * mm, "end": v(36.28, -11.1) * mm});
            skSolve(sketch);
        }
        {
            var Q0;
            {var subQ0=sQuery(id+"F60.wireOp",EDGE,"E111");Q0=makeQuery(id+"F60.imprint","IMPRINT",FACE,{"disambiguationData":[TD([[makeQuery(id+"F60.imprint","IMPRINT",EDGE,{"derivedFrom":subQ0}),1.0]])]});}
            extrude(context, id + "F61", {"entities" : qUnion([Q0]), "operationType" : NewBodyOperationType.REMOVE, "oppositeDirection" : true, "depth" : 25 * mm});
        }
        {
            var Q0;
            {var subQ0=sQuery(id+"F60.wireOp",EDGE,"E113");Q0=makeQuery(id+"F60.imprint","IMPRINT",FACE,{"disambiguationData":[TD([[makeQuery(id+"F60.imprint","IMPRINT",EDGE,{"derivedFrom":subQ0}),1.0]])]});}
            extrude(context, id + "F62", {"entities" : qUnion([Q0]), "operationType" : NewBodyOperationType.REMOVE, "oppositeDirection" : true, "depth" : 25 * mm});
        }
        {
            var Q0;
            Q0=makeQuery(id+"F57.boolean.opBoolean","MERGE",FACE,{"derivedFrom":[makeQuery(id+"F49.opExtrude","SWEPT_FACE",FACE,{"disambiguationData":[OSD([sQuery(id+"F48.wireOp",EDGE,"E88")])]}),makeQuery(id+"F57.opExtrude","SWEPT_FACE",FACE,{"disambiguationData":[OSD([sQuery(id+"F56.wireOp",EDGE,"E104.bottom")])]})]});
            var sketch = newSketch(context, id + "F63", { "sketchPlane" : qUnion([Q0])});
            skLineSegment(sketch, "E139.bottom", {"start": v(-6.08, -1.05) * mm, "end": v(18.75, -1.05) * mm});
            skLineSegment(sketch, "E139.top", {"start": v(-6.5, -10.81) * mm, "end": v(18.75, -10.81) * mm});
            skLineSegment(sketch, "E139.left", {"start": v(-8.17, -3.15) * mm, "end": v(-8.17, -9.14) * mm});
            skLineSegment(sketch, "E139.right", {"start": v(20.84, -3.15) * mm, "end": v(20.84, -8.72) * mm});
            skPoint(sketch, "E140.visualSharp", {"position": v(-8.17, -1.05) * mm});
            skArc(sketch, "E140.filletArc", {"start": v(-6.08, -1.05) * mm, "mid": v(-7.56, -1.67) * mm, "end": v(-8.17, -3.15) * mm});
            skPoint(sketch, "E141.visualSharp", {"position": v(-8.17, -10.81) * mm});
            skArc(sketch, "E141.filletArc", {"start": v(-8.17, -9.14) * mm, "mid": v(-7.68, -10.32) * mm, "end": v(-6.5, -10.81) * mm});
            skPoint(sketch, "E142.visualSharp", {"position": v(20.84, -10.81) * mm});
            skArc(sketch, "E142.filletArc", {"start": v(18.75, -10.81) * mm, "mid": v(20.23, -10.2) * mm, "end": v(20.84, -8.72) * mm});
            skPoint(sketch, "E143.visualSharp", {"position": v(20.84, -1.05) * mm});
            skArc(sketch, "E143.filletArc", {"start": v(20.84, -3.15) * mm, "mid": v(20.23, -1.67) * mm, "end": v(18.75, -1.05) * mm});
            skSolve(sketch);
        }
        {
            var Q0;
            Q0=makeQuery(id+"F63.imprint","IMPRINT",FACE,{"disambiguationData":[TD([[makeQuery(id+"F63.imprint","IMPRINT",EDGE,{"derivedFrom":sQuery(id+"F63.wireOp",EDGE,"E139.bottom")}),-1.0]])]});
            extrude(context, id + "F64", {"entities" : qUnion([Q0]), "operationType" : NewBodyOperationType.REMOVE, "oppositeDirection" : true, "depth" : 25 * mm});
        }
        {
            var Q0;
            Q0=makeQuery(id+"F3.boolean.opBoolean","COPY",FACE,{"derivedFrom":makeQuery(id+"F3.opExtrude","CAP_FACE",FACE,{"disambiguationData":[OSD([sQuery(id+"F2.wireOp",EDGE,"E4.bottom"),sQuery(id+"F2.wireOp",EDGE,"E4.top"),sQuery(id+"F2.wireOp",EDGE,"E4.left"),sQuery(id+"F2.wireOp",EDGE,"E4.right")])],"isStart":false})});
            var sketch = newSketch(context, id + "F65", { "sketchPlane" : qUnion([Q0])});
            skLineSegment(sketch, "E144.bottom", {"start": v(-5.95, 16.02) * mm, "end": v(11.17, 16.02) * mm});
            skLineSegment(sketch, "E144.top", {"start": v(-5.95, 10.62) * mm, "end": v(11.17, 10.62) * mm});
            skLineSegment(sketch, "E144.left", {"start": v(-5.95, 16.02) * mm, "end": v(-5.95, 10.62) * mm});
            skLineSegment(sketch, "E144.right", {"start": v(11.17, 16.02) * mm, "end": v(11.17, 10.62) * mm});
            skSolve(sketch);
        }
        {
            var Q0;
            Q0=makeQuery(id+"F65.imprint","IMPRINT",FACE,{"disambiguationData":[TD([[makeQuery(id+"F65.imprint","IMPRINT",EDGE,{"derivedFrom":sQuery(id+"F65.wireOp",EDGE,"E144.bottom")}),-1.0]])]});
            extrude(context, id + "F66", {"entities" : qUnion([Q0]), "operationType" : NewBodyOperationType.REMOVE, "oppositeDirection" : true, "depth" : 10 * mm});
        }
        {
            var Q0;
            Q0=makeQuery(id+"F57.boolean.opBoolean","MERGE",FACE,{"derivedFrom":[makeQuery(id+"F49.opExtrude","SWEPT_FACE",FACE,{"disambiguationData":[OSD([sQuery(id+"F48.wireOp",EDGE,"E88")])]}),makeQuery(id+"F57.opExtrude","SWEPT_FACE",FACE,{"disambiguationData":[OSD([sQuery(id+"F56.wireOp",EDGE,"E104.bottom")])]})]});
            var sketch = newSketch(context, id + "F67", { "sketchPlane" : qUnion([Q0])});
            skLineSegment(sketch, "E145", {"start": v(-33.93, -8.07) * mm, "end": v(-39.2, -6.93) * mm});
            skLineSegment(sketch, "E146", {"start": v(-45.77, -5.92) * mm, "end": v(-53.9, -5.16) * mm});
            skLineSegment(sketch, "E147", {"start": v(-54.85, -4.64) * mm, "end": v(-56.18, -2.94) * mm});
            skLineSegment(sketch, "E148", {"start": v(-56.18, -2.94) * mm, "end": v(-56.18, -2.93) * mm});
            skLineSegment(sketch, "E149", {"start": v(-54.38, -0.19) * mm, "end": v(-50.66, 1.43) * mm});
            skLineSegment(sketch, "E150", {"start": v(-50.02, 1.63) * mm, "end": v(-35.2, 4.41) * mm});
            skLineSegment(sketch, "E151", {"start": v(-32.55, 4.03) * mm, "end": v(-29.84, 2.65) * mm});
            skLineSegment(sketch, "E152", {"start": v(-28.22, 1.18) * mm, "end": v(-26.58, -1.4) * mm});
            skLineSegment(sketch, "E153", {"start": v(-26, -4.33) * mm, "end": v(-26.2, -5.55) * mm});
            skLineSegment(sketch, "E154", {"start": v(-28.65, -8.04) * mm, "end": v(-29.17, -8.13) * mm});
            skPoint(sketch, "E155.visualSharp", {"position": v(-56.18, -0.97) * mm});
            skArc(sketch, "E155.filletArc", {"start": v(-54.38, -0.19) * mm, "mid": v(-55.69, -1.3) * mm, "end": v(-56.18, -2.93) * mm});
            skPoint(sketch, "E156.visualSharp", {"position": v(-50.35, 1.57) * mm});
            skArc(sketch, "E156.filletArc", {"start": v(-50.02, 1.63) * mm, "mid": v(-50.34, 1.55) * mm, "end": v(-50.66, 1.43) * mm});
            skPoint(sketch, "E157.visualSharp", {"position": v(-33.8, 4.67) * mm});
            skArc(sketch, "E157.filletArc", {"start": v(-32.55, 4.03) * mm, "mid": v(-33.84, 4.44) * mm, "end": v(-35.2, 4.41) * mm});
            skPoint(sketch, "E158.visualSharp", {"position": v(-28.83, 2.13) * mm});
            skArc(sketch, "E158.filletArc", {"start": v(-28.22, 1.18) * mm, "mid": v(-28.93, 2.02) * mm, "end": v(-29.84, 2.65) * mm});
            skPoint(sketch, "E159.visualSharp", {"position": v(-25.72, -2.76) * mm});
            skArc(sketch, "E159.filletArc", {"start": v(-26, -4.33) * mm, "mid": v(-26.02, -2.81) * mm, "end": v(-26.58, -1.4) * mm});
            skPoint(sketch, "E160.visualSharp", {"position": v(-26.57, -7.64) * mm});
            skArc(sketch, "E160.filletArc", {"start": v(-28.65, -8.04) * mm, "mid": v(-27.04, -7.18) * mm, "end": v(-26.2, -5.55) * mm});
            skPoint(sketch, "E161.visualSharp", {"position": v(-31.55, -8.58) * mm});
            skArc(sketch, "E161.filletArc", {"start": v(-33.93, -8.07) * mm, "mid": v(-31.55, -8.34) * mm, "end": v(-29.17, -8.13) * mm});
            skPoint(sketch, "E162.visualSharp", {"position": v(-42.46, -6.23) * mm});
            skArc(sketch, "E162.filletArc", {"start": v(-39.2, -6.93) * mm, "mid": v(-42.47, -6.33) * mm, "end": v(-45.77, -5.92) * mm});
            skPoint(sketch, "E163.visualSharp", {"position": v(-54.49, -5.1) * mm});
            skArc(sketch, "E163.filletArc", {"start": v(-54.85, -4.64) * mm, "mid": v(-54.43, -5) * mm, "end": v(-53.9, -5.16) * mm});
            skLineSegment(sketch, "E164", {"start": v(38.18, -0.62) * mm, "end": v(22.31, -0.62) * mm});
            skLineSegment(sketch, "E165", {"start": v(22.31, -0.62) * mm, "end": v(21.57, -1.04) * mm});
            skLineSegment(sketch, "E166", {"start": v(21.57, -1.04) * mm, "end": v(21.34, -1.7) * mm});
            skLineSegment(sketch, "E167", {"start": v(21.2, -2.52) * mm, "end": v(21.2, -3.05) * mm});
            skLineSegment(sketch, "E168", {"start": v(21.2, -3.05) * mm, "end": v(21.78, -3.84) * mm});
            skLineSegment(sketch, "E169", {"start": v(21.78, -3.84) * mm, "end": v(23.37, -6) * mm});
            skLineSegment(sketch, "E170", {"start": v(23.37, -6) * mm, "end": v(24.05, -7.59) * mm});
            skLineSegment(sketch, "E171", {"start": v(24.16, -8.12) * mm, "end": v(24.16, -10.91) * mm});
            skLineSegment(sketch, "E172", {"start": v(23.75, -11.89) * mm, "end": v(23.13, -12.5) * mm});
            skLineSegment(sketch, "E173", {"start": v(21.78, -15.69) * mm, "end": v(21.78, -16.07) * mm});
            skLineSegment(sketch, "E174", {"start": v(21.78, -16.07) * mm, "end": v(24.17, -16.6) * mm});
            skLineSegment(sketch, "E175", {"start": v(25.68, -16.44) * mm, "end": v(30.15, -14.5) * mm});
            skLineSegment(sketch, "E176", {"start": v(35.19, -10.84) * mm, "end": v(40.14, -5.24) * mm});
            skLineSegment(sketch, "E177", {"start": v(40.47, -4.55) * mm, "end": v(40.65, -3.55) * mm});
            skLineSegment(sketch, "E178", {"start": v(39.87, -1.28) * mm, "end": v(39.85, -1.27) * mm});
            skPoint(sketch, "E179.visualSharp", {"position": v(24.16, -7.85) * mm});
            skArc(sketch, "E179.filletArc", {"start": v(24.16, -8.12) * mm, "mid": v(24.13, -7.85) * mm, "end": v(24.05, -7.59) * mm});
            skPoint(sketch, "E180.visualSharp", {"position": v(24.16, -11.49) * mm});
            skArc(sketch, "E180.filletArc", {"start": v(23.75, -11.89) * mm, "mid": v(24.05, -11.44) * mm, "end": v(24.16, -10.91) * mm});
            skPoint(sketch, "E181.visualSharp", {"position": v(21.78, -13.8) * mm});
            skArc(sketch, "E181.filletArc", {"start": v(23.13, -12.5) * mm, "mid": v(22.13, -13.95) * mm, "end": v(21.78, -15.69) * mm});
            skPoint(sketch, "E182.visualSharp", {"position": v(24.95, -16.76) * mm});
            skArc(sketch, "E182.filletArc", {"start": v(24.17, -16.6) * mm, "mid": v(24.94, -16.64) * mm, "end": v(25.68, -16.44) * mm});
            skPoint(sketch, "E183.visualSharp", {"position": v(33.07, -13.23) * mm});
            skArc(sketch, "E183.filletArc", {"start": v(30.15, -14.5) * mm, "mid": v(32.87, -12.94) * mm, "end": v(35.19, -10.84) * mm});
            skPoint(sketch, "E184.visualSharp", {"position": v(40.4, -4.94) * mm});
            skArc(sketch, "E184.filletArc", {"start": v(40.14, -5.24) * mm, "mid": v(40.36, -4.92) * mm, "end": v(40.47, -4.55) * mm});
            skPoint(sketch, "E185.visualSharp", {"position": v(40.88, -2.2) * mm});
            skArc(sketch, "E185.filletArc", {"start": v(40.65, -3.55) * mm, "mid": v(40.55, -2.32) * mm, "end": v(39.87, -1.28) * mm});
            skPoint(sketch, "E186.visualSharp", {"position": v(39.14, -0.62) * mm});
            skArc(sketch, "E186.filletArc", {"start": v(39.85, -1.27) * mm, "mid": v(39.07, -0.79) * mm, "end": v(38.18, -0.62) * mm});
            skPoint(sketch, "E187.visualSharp", {"position": v(21.2, -2.1) * mm});
            skArc(sketch, "E187.filletArc", {"start": v(21.34, -1.7) * mm, "mid": v(21.24, -2.1) * mm, "end": v(21.2, -2.52) * mm});
            skSolve(sketch);
        }
        {
            var Q0;
            Q0=makeQuery(id+"F67.imprint","IMPRINT",FACE,{"disambiguationData":[TD([[makeQuery(id+"F67.imprint","IMPRINT",EDGE,{"derivedFrom":sQuery(id+"F67.wireOp",EDGE,"E145")}),-1.0]])]});
            extrude(context, id + "F68", {"entities" : qUnion([Q0]), "operationType" : NewBodyOperationType.REMOVE, "oppositeDirection" : true, "depth" : 25 * mm});
        }
        {
            var Q0;
            Q0=makeQuery(id+"F67.imprint","IMPRINT",FACE,{"disambiguationData":[TD([[makeQuery(id+"F67.imprint","IMPRINT",EDGE,{"derivedFrom":sQuery(id+"F67.wireOp",EDGE,"E164")}),1.0]])]});
            extrude(context, id + "F69", {"entities" : qUnion([Q0]), "operationType" : NewBodyOperationType.REMOVE, "oppositeDirection" : true, "depth" : 25 * mm});
        }
        {
            var Q0;
            Q0=makeQuery(id+"F28.boolean.opBoolean","MERGE",FACE,{"derivedFrom":[makeQuery(id+"F24.opExtrude","CAP_FACE",FACE,{"disambiguationData":[OSD([sQuery(id+"F19.wireOp",EDGE,"E29"),sQuery(id+"F19.wireOp",EDGE,"E30"),sQuery(id+"F19.wireOp",EDGE,"E31"),sQuery(id+"F19.wireOp",EDGE,"E32"),sQuery(id+"F19.wireOp",EDGE,"E33.filletArc"),sQuery(id+"F19.wireOp",EDGE,"E34.filletArc")])],"isStart":false}),makeQuery(id+"F28.opExtrude","SWEPT_FACE",FACE,{"disambiguationData":[OSD([sQuery(id+"F27.wireOp",EDGE,"E51")])]})]});
            var sketch = newSketch(context, id + "F70", { "sketchPlane" : qUnion([Q0])});
            skCircle(sketch, "E188", {"center": v(37.2, 33.62) * mm, "radius": 0.82 * mm});
            skCircle(sketch, "E189", {"center": v(37.2, -6.03) * mm, "radius": 0.78 * mm});
            skSolve(sketch);
        }
        {
            var Q0;
            Q0 = qSketchRegion(id + "F70", true);
            extrude(context, id + "F71", {"entities" : qUnion([Q0]), "operationType" : NewBodyOperationType.REMOVE, "oppositeDirection" : true, "depth" : 25 * mm});
        }
        {
            var Q0;
            Q0=makeQuery(id+"F45.boolean.opBoolean","COPY",FACE,{"derivedFrom":makeQuery(id+"F45.opExtrude","SWEPT_FACE",FACE,{"disambiguationData":[OSD([sQuery(id+"F44.wireOp",EDGE,"E79")])]})});
            var sketch = newSketch(context, id + "F72", { "sketchPlane" : qUnion([Q0])});
            skLineSegment(sketch, "E190", {"start": v(11.42, 13) * mm, "end": v(11.42, 5.6) * mm});
            skLineSegment(sketch, "E191", {"start": v(11.42, 5.6) * mm, "end": v(25.82, 5.6) * mm});
            skLineSegment(sketch, "E192", {"start": v(25.82, 5.6) * mm, "end": v(25.82, 13) * mm});
            skLineSegment(sketch, "E193", {"start": v(25.82, 13) * mm, "end": v(11.42, 13) * mm});
            skSolve(sketch);
        }
        {
            var Q0;
            Q0 = qSketchRegion(id + "F72", true);
            extrude(context, id + "F73", {"entities" : qUnion([Q0]), "operationType" : NewBodyOperationType.ADD, "depth" : 2 * mm});
        }
        {
            var Q0;
            Q0=makeQuery(id+"F43.boolean.opBoolean","COPY",FACE,{"derivedFrom":makeQuery(id+"F43.opExtrude","SWEPT_FACE",FACE,{"disambiguationData":[OSD([sQuery(id+"F42.wireOp",EDGE,"E73")])]})});
            var sketch = newSketch(context, id + "F74", { "sketchPlane" : qUnion([Q0])});
            skLineSegment(sketch, "E194", {"start": v(-2.34, 13) * mm, "end": v(-2.33, 5.6) * mm});
            skLineSegment(sketch, "E195", {"start": v(-2.33, 5.6) * mm, "end": v(12.2, 5.61) * mm});
            skLineSegment(sketch, "E196", {"start": v(12.2, 5.61) * mm, "end": v(12.2, 13) * mm});
            skLineSegment(sketch, "E197", {"start": v(12.2, 13) * mm, "end": v(-2.34, 13) * mm});
            skSolve(sketch);
        }
        {
            var Q0;
            Q0 = qSketchRegion(id + "F74", true);
            extrude(context, id + "F75", {"entities" : qUnion([Q0]), "operationType" : NewBodyOperationType.ADD, "depth" : 2 * mm});
        }
        {
            var Q0;
            Q0=makeQuery(id+"F73.opExtrude","SWEPT_FACE",FACE,{"disambiguationData":[OSD([sQuery(id+"F72.wireOp",EDGE,"E190")])]});
            var sketch = newSketch(context, id + "F76", { "sketchPlane" : qUnion([Q0])});
            skSolve(sketch);
        }
        {
            var Q0;
            {var subQ0=sQuery(id+"F72.wireOp",EDGE,"E190");Q0=makeQuery(id+"F76.imprint","IMPRINT",FACE,{"disambiguationData":[TD([[makeQuery(id+"F76.imprint","IMPRINT",EDGE,{"derivedFrom":makeQuery(id+"F73.opExtrude","CAP_EDGE",EDGE,{"disambiguationData":[OSD([subQ0])],"isStart":false})}),-1.0]])]});}
            extrude(context, id + "F77", {"entities" : qUnion([Q0]), "operationType" : NewBodyOperationType.ADD, "depth" : 25 * mm});
        }
        {
            var Q0;
            Q0=makeQuery(id+"F75.opExtrude","SWEPT_FACE",FACE,{"disambiguationData":[OSD([sQuery(id+"F74.wireOp",EDGE,"E196")])]});
            extrude(context, id + "F78", {"entities" : qUnion([Q0]), "operationType" : NewBodyOperationType.ADD, "depth" : 25 * mm});
        }
        {
            var Q0;
            Q0=makeQuery(id+"F1.opExtrude","SWEPT_FACE",FACE,{"disambiguationData":[OSD([sQuery(id+"F0.wireOp",EDGE,"E1")])]});
            var sketch = newSketch(context, id + "F79", { "sketchPlane" : qUnion([Q0])});
            skLineSegment(sketch, "E198.bottom", {"start": v(-20.7, 12.14) * mm, "end": v(-24.32, 12.14) * mm});
            skLineSegment(sketch, "E198.top", {"start": v(-20.7, 11.07) * mm, "end": v(-24.32, 11.07) * mm});
            skLineSegment(sketch, "E198.left", {"start": v(-20.7, 12.14) * mm, "end": v(-20.7, 11.07) * mm});
            skLineSegment(sketch, "E198.right", {"start": v(-24.32, 12.14) * mm, "end": v(-24.32, 11.07) * mm});
            skSolve(sketch);
        }
        {
            var Q0;
            Q0 = qSketchRegion(id + "F79", true);
            extrude(context, id + "F80", {"entities" : qUnion([Q0]), "operationType" : NewBodyOperationType.REMOVE, "oppositeDirection" : true, "depth" : 28 * mm});
        }
        {
            var Q0;
            {var subQ0=sQuery(id+"F74.wireOp",EDGE,"E197");var subQ1=sQuery(id+"F0.wireOp",EDGE,"E0");var subQ2=sQuery(id+"F0.wireOp",EDGE,"E2");var subQ3=sQuery(id+"F0.wireOp",EDGE,"E3");Q0=makeQuery(id+"F78.boolean.opBoolean","MERGE",FACE,{"derivedFrom":[makeQuery(id+"F75.boolean.opBoolean","MERGE",FACE,{"derivedFrom":[makeQuery(id+"F39.boolean.opBoolean","MERGE",FACE,{"derivedFrom":[makeQuery(id+"F9.boolean.opBoolean","MERGE",FACE,{"derivedFrom":[makeQuery(id+"F3.boolean.opBoolean","SPLIT",FACE,{"disambiguationData":[TD([makeQuery(id+"F1.opExtrude","SWEPT_FACE",FACE,{"disambiguationData":[OSD([subQ3])]})])],"derivedFrom":makeQuery(id+"F1.opExtrude","CAP_FACE",FACE,{"disambiguationData":[OSD([subQ1,sQuery(id+"F0.wireOp",EDGE,"E1"),subQ2,subQ3])],"isStart":false})}),makeQuery(id+"F9.opExtrude","SWEPT_FACE",FACE,{"disambiguationData":[OSD([sQuery(id+"F8.wireOp",EDGE,"E16")])]})]}),makeQuery(id+"F39.opExtrude","SWEPT_FACE",FACE,{"disambiguationData":[OSD([sQuery(id+"F38.wireOp",EDGE,"E71.bottom")])]})]}),makeQuery(id+"F75.opExtrude","SWEPT_FACE",FACE,{"disambiguationData":[OSD([subQ0])]})]}),makeQuery(id+"F78.opExtrude","SWEPT_FACE",FACE,{"disambiguationData":[OSD([sQuery(id+"F74.wireOp",EDGE,"E196"),subQ0])]})]});}
            var sketch = newSketch(context, id + "F81", { "sketchPlane" : qUnion([Q0])});
            skLineSegment(sketch, "E199", {"start": v(74.17, 26.9) * mm, "end": v(69.73, 26.9) * mm});
            skLineSegment(sketch, "E200", {"start": v(69.73, 26.9) * mm, "end": v(69.73, 16.02) * mm});
            skLineSegment(sketch, "E201", {"start": v(69.73, 16.02) * mm, "end": v(74.17, 16.02) * mm});
            skLineSegment(sketch, "E202", {"start": v(74.17, 16.02) * mm, "end": v(74.17, 26.9) * mm});
            skSolve(sketch);
        }
        {
            var Q0;
            Q0 = qSketchRegion(id + "F81", true);
            extrude(context, id + "F82", {"entities" : qUnion([Q0]), "operationType" : NewBodyOperationType.ADD, "depth" : 7 * mm});
        }
        {
            var Q0;
            {var subQ0=sQuery(id+"F72.wireOp",EDGE,"E193");var subQ1=sQuery(id+"F0.wireOp",EDGE,"E0");var subQ2=sQuery(id+"F0.wireOp",EDGE,"E1");var subQ3=sQuery(id+"F0.wireOp",EDGE,"E2");Q0=makeQuery(id+"F77.boolean.opBoolean","MERGE",FACE,{"derivedFrom":[makeQuery(id+"F73.boolean.opBoolean","MERGE",FACE,{"derivedFrom":[makeQuery(id+"F41.boolean.opBoolean","MERGE",FACE,{"derivedFrom":[makeQuery(id+"F37.boolean.opBoolean","MERGE",FACE,{"derivedFrom":[makeQuery(id+"F7.boolean.opBoolean","MERGE",FACE,{"derivedFrom":[makeQuery(id+"F3.boolean.opBoolean","SPLIT",FACE,{"disambiguationData":[TD([makeQuery(id+"F1.opExtrude","SWEPT_FACE",FACE,{"disambiguationData":[OSD([subQ2])]})])],"derivedFrom":makeQuery(id+"F1.opExtrude","CAP_FACE",FACE,{"disambiguationData":[OSD([subQ1,subQ2,subQ3,sQuery(id+"F0.wireOp",EDGE,"E3")])],"isStart":false})}),makeQuery(id+"F7.opExtrude","SWEPT_FACE",FACE,{"disambiguationData":[OSD([sQuery(id+"F6.wireOp",EDGE,"E12")])]})]}),makeQuery(id+"F37.opExtrude","SWEPT_FACE",FACE,{"disambiguationData":[OSD([sQuery(id+"F36.wireOp",EDGE,"E70.bottom")])]})]}),makeQuery(id+"F41.opExtrude","SWEPT_FACE",FACE,{"disambiguationData":[OSD([sQuery(id+"F40.wireOp",EDGE,"E72.bottom")])]})]}),makeQuery(id+"F73.opExtrude","SWEPT_FACE",FACE,{"disambiguationData":[OSD([subQ0])]})]}),makeQuery(id+"F77.opExtrude","SWEPT_FACE",FACE,{"disambiguationData":[OSD([sQuery(id+"F72.wireOp",EDGE,"E190"),subQ0])]})]});}
            var sketch = newSketch(context, id + "F83", { "sketchPlane" : qUnion([Q0])});
            skLineSegment(sketch, "E203", {"start": v(69.79, 10.62) * mm, "end": v(69.79, 0) * mm});
            skLineSegment(sketch, "E204", {"start": v(69.79, 0) * mm, "end": v(74.17, 0) * mm});
            skLineSegment(sketch, "E205", {"start": v(74.17, 0) * mm, "end": v(74.17, 10.62) * mm});
            skLineSegment(sketch, "E206", {"start": v(74.17, 10.62) * mm, "end": v(69.79, 10.62) * mm});
            skSolve(sketch);
        }
        {
            var Q0;
            Q0 = qSketchRegion(id + "F83", true);
            extrude(context, id + "F84", {"entities" : qUnion([Q0]), "operationType" : NewBodyOperationType.ADD, "depth" : 7 * mm});
        }
        {
            var Q0;
            {var subQ0=sQuery(id+"F72.wireOp",EDGE,"E193");var subQ1=sQuery(id+"F0.wireOp",EDGE,"E0");var subQ2=sQuery(id+"F0.wireOp",EDGE,"E1");var subQ3=sQuery(id+"F0.wireOp",EDGE,"E2");Q0=makeQuery(id+"F77.boolean.opBoolean","MERGE",FACE,{"derivedFrom":[makeQuery(id+"F73.boolean.opBoolean","MERGE",FACE,{"derivedFrom":[makeQuery(id+"F41.boolean.opBoolean","MERGE",FACE,{"derivedFrom":[makeQuery(id+"F37.boolean.opBoolean","MERGE",FACE,{"derivedFrom":[makeQuery(id+"F7.boolean.opBoolean","MERGE",FACE,{"derivedFrom":[makeQuery(id+"F3.boolean.opBoolean","SPLIT",FACE,{"disambiguationData":[TD([makeQuery(id+"F1.opExtrude","SWEPT_FACE",FACE,{"disambiguationData":[OSD([subQ2])]})])],"derivedFrom":makeQuery(id+"F1.opExtrude","CAP_FACE",FACE,{"disambiguationData":[OSD([subQ1,subQ2,subQ3,sQuery(id+"F0.wireOp",EDGE,"E3")])],"isStart":false})}),makeQuery(id+"F7.opExtrude","SWEPT_FACE",FACE,{"disambiguationData":[OSD([sQuery(id+"F6.wireOp",EDGE,"E12")])]})]}),makeQuery(id+"F37.opExtrude","SWEPT_FACE",FACE,{"disambiguationData":[OSD([sQuery(id+"F36.wireOp",EDGE,"E70.bottom")])]})]}),makeQuery(id+"F41.opExtrude","SWEPT_FACE",FACE,{"disambiguationData":[OSD([sQuery(id+"F40.wireOp",EDGE,"E72.bottom")])]})]}),makeQuery(id+"F73.opExtrude","SWEPT_FACE",FACE,{"disambiguationData":[OSD([subQ0])]})]}),makeQuery(id+"F77.opExtrude","SWEPT_FACE",FACE,{"disambiguationData":[OSD([sQuery(id+"F72.wireOp",EDGE,"E190"),subQ0])]})]});}
            var sketch = newSketch(context, id + "F85", { "sketchPlane" : qUnion([Q0])});
            skLineSegment(sketch, "E207", {"start": v(62.33, -37.63) * mm, "end": v(60.97, -39.19) * mm});
            skLineSegment(sketch, "E208", {"start": v(60.97, -39.19) * mm, "end": v(60.45, -36.94) * mm});
            skLineSegment(sketch, "E209", {"start": v(60.45, -36.94) * mm, "end": v(62.33, -37.63) * mm});
            skSolve(sketch);
        }
        {
            var Q0;
            Q0 = qSketchRegion(id + "F85", true);
            extrude(context, id + "F86", {"entities" : qUnion([Q0]), "operationType" : NewBodyOperationType.ADD, "oppositeDirection" : true, "depth" : 7.5 * mm});
        }
        {
            var Q0;
            Q0=makeQuery(id+"F86.opExtrude","SWEPT_FACE",FACE,{"disambiguationData":[OSD([sQuery(id+"F85.wireOp",EDGE,"E208")])]});
            var sketch = newSketch(context, id + "F87", { "sketchPlane" : qUnion([Q0])});
            skSolve(sketch);
        }
        {
            var Q0;
            {var subQ0=sQuery(id+"F85.wireOp",EDGE,"E208");Q0=makeQuery(id+"F87.imprint","IMPRINT",FACE,{"disambiguationData":[TD([[makeQuery(id+"F87.imprint","IMPRINT",EDGE,{"derivedFrom":makeQuery(id+"F86.opExtrude","CAP_EDGE",EDGE,{"disambiguationData":[OSD([subQ0])],"isStart":true})}),1.0]])]});}
            extrude(context, id + "F88", {"entities" : qUnion([Q0]), "operationType" : NewBodyOperationType.ADD, "depth" : 5 * mm});
        }
        {
            var Q0;
            {var subQ0=sQuery(id+"F74.wireOp",EDGE,"E197");var subQ1=sQuery(id+"F0.wireOp",EDGE,"E0");var subQ2=sQuery(id+"F0.wireOp",EDGE,"E2");var subQ3=sQuery(id+"F0.wireOp",EDGE,"E3");Q0=makeQuery(id+"F78.boolean.opBoolean","MERGE",FACE,{"derivedFrom":[makeQuery(id+"F75.boolean.opBoolean","MERGE",FACE,{"derivedFrom":[makeQuery(id+"F39.boolean.opBoolean","MERGE",FACE,{"derivedFrom":[makeQuery(id+"F9.boolean.opBoolean","MERGE",FACE,{"derivedFrom":[makeQuery(id+"F3.boolean.opBoolean","SPLIT",FACE,{"disambiguationData":[TD([makeQuery(id+"F1.opExtrude","SWEPT_FACE",FACE,{"disambiguationData":[OSD([subQ3])]})])],"derivedFrom":makeQuery(id+"F1.opExtrude","CAP_FACE",FACE,{"disambiguationData":[OSD([subQ1,sQuery(id+"F0.wireOp",EDGE,"E1"),subQ2,subQ3])],"isStart":false})}),makeQuery(id+"F9.opExtrude","SWEPT_FACE",FACE,{"disambiguationData":[OSD([sQuery(id+"F8.wireOp",EDGE,"E16")])]})]}),makeQuery(id+"F39.opExtrude","SWEPT_FACE",FACE,{"disambiguationData":[OSD([sQuery(id+"F38.wireOp",EDGE,"E71.bottom")])]})]}),makeQuery(id+"F75.opExtrude","SWEPT_FACE",FACE,{"disambiguationData":[OSD([subQ0])]})]}),makeQuery(id+"F78.opExtrude","SWEPT_FACE",FACE,{"disambiguationData":[OSD([sQuery(id+"F74.wireOp",EDGE,"E196"),subQ0])]})]});}
            var sketch = newSketch(context, id + "F89", { "sketchPlane" : qUnion([Q0])});
            skLineSegment(sketch, "E210", {"start": v(61.46, 64.38) * mm, "end": v(60.15, 65.75) * mm});
            skLineSegment(sketch, "E211", {"start": v(60.15, 65.75) * mm, "end": v(59.6, 63.64) * mm});
            skLineSegment(sketch, "E212", {"start": v(59.6, 63.64) * mm, "end": v(61.46, 64.38) * mm});
            skSolve(sketch);
        }
        {
            var Q0;
            Q0 = qSketchRegion(id + "F89", true);
            extrude(context, id + "F90", {"entities" : qUnion([Q0]), "operationType" : NewBodyOperationType.ADD, "oppositeDirection" : true, "depth" : 7.5 * mm});
        }
        {
            var Q0;
            Q0=makeQuery(id+"F90.opExtrude","SWEPT_FACE",FACE,{"disambiguationData":[OSD([sQuery(id+"F89.wireOp",EDGE,"E211")])]});
            var sketch = newSketch(context, id + "F91", { "sketchPlane" : qUnion([Q0])});
            skSolve(sketch);
        }
        {
            var Q0;
            {var subQ0=sQuery(id+"F89.wireOp",EDGE,"E211");Q0=makeQuery(id+"F91.imprint","IMPRINT",FACE,{"disambiguationData":[TD([[makeQuery(id+"F91.imprint","IMPRINT",EDGE,{"derivedFrom":makeQuery(id+"F90.opExtrude","CAP_EDGE",EDGE,{"disambiguationData":[OSD([subQ0])],"isStart":true})}),-1.0]])]});}
            extrude(context, id + "F92", {"entities" : qUnion([Q0]), "operationType" : NewBodyOperationType.ADD, "depth" : 5 * mm});
        }
        {
            var Q0;
            Q0=makeQuery(id+"F88.opExtrude","SWEPT_FACE",FACE,{"disambiguationData":[OSD([sQuery(id+"F44.wireOp",EDGE,"E79"),sQuery(id+"F44.wireOp",EDGE,"E80"),sQuery(id+"F44.wireOp",EDGE,"E82"),sQuery(id+"F44.wireOp",EDGE,"E84"),sQuery(id+"F72.wireOp",EDGE,"E190"),sQuery(id+"F72.wireOp",EDGE,"E193"),sQuery(id+"F85.wireOp",EDGE,"E208"),sQuery(id+"F85.wireOp",EDGE,"E209")])]});
            var sketch = newSketch(context, id + "F93", { "sketchPlane" : qUnion([Q0])});
            skCircle(sketch, "E213", {"center": v(-48.38, 9.3) * mm, "radius": 0.72 * mm});
            skPoint(sketch, "E213.centerSnap0", {"position": v(-50.6, 9.3) * mm});
            skCircle(sketch, "E214", {"center": v(88.84, 196.9) * mm, "radius": 0.78 * mm});
            skSolve(sketch);
        }
        {
            var Q0;
            Q0 = qSketchRegion(id + "F93", true);
            extrude(context, id + "F94", {"entities" : qUnion([Q0]), "operationType" : NewBodyOperationType.REMOVE, "oppositeDirection" : true, "depth" : 25 * mm});
        }
        {
            var Q0;
            Q0=makeQuery(id+"F92.opExtrude","SWEPT_FACE",FACE,{"disambiguationData":[OSD([sQuery(id+"F42.wireOp",EDGE,"E73"),sQuery(id+"F42.wireOp",EDGE,"E74"),sQuery(id+"F42.wireOp",EDGE,"E76"),sQuery(id+"F42.wireOp",EDGE,"E78"),sQuery(id+"F74.wireOp",EDGE,"E196"),sQuery(id+"F74.wireOp",EDGE,"E197"),sQuery(id+"F89.wireOp",EDGE,"E211"),sQuery(id+"F89.wireOp",EDGE,"E212")])]});
            var sketch = newSketch(context, id + "F95", { "sketchPlane" : qUnion([Q0])});
            skCircle(sketch, "E215", {"center": v(38.91, 9.42) * mm, "radius": 0.76 * mm});
            skSolve(sketch);
        }
        {
            var Q0;
            Q0 = qSketchRegion(id + "F95", true);
            extrude(context, id + "F96", {"entities" : qUnion([Q0]), "operationType" : NewBodyOperationType.REMOVE, "oppositeDirection" : true, "depth" : 25 * mm});
        }
    });
